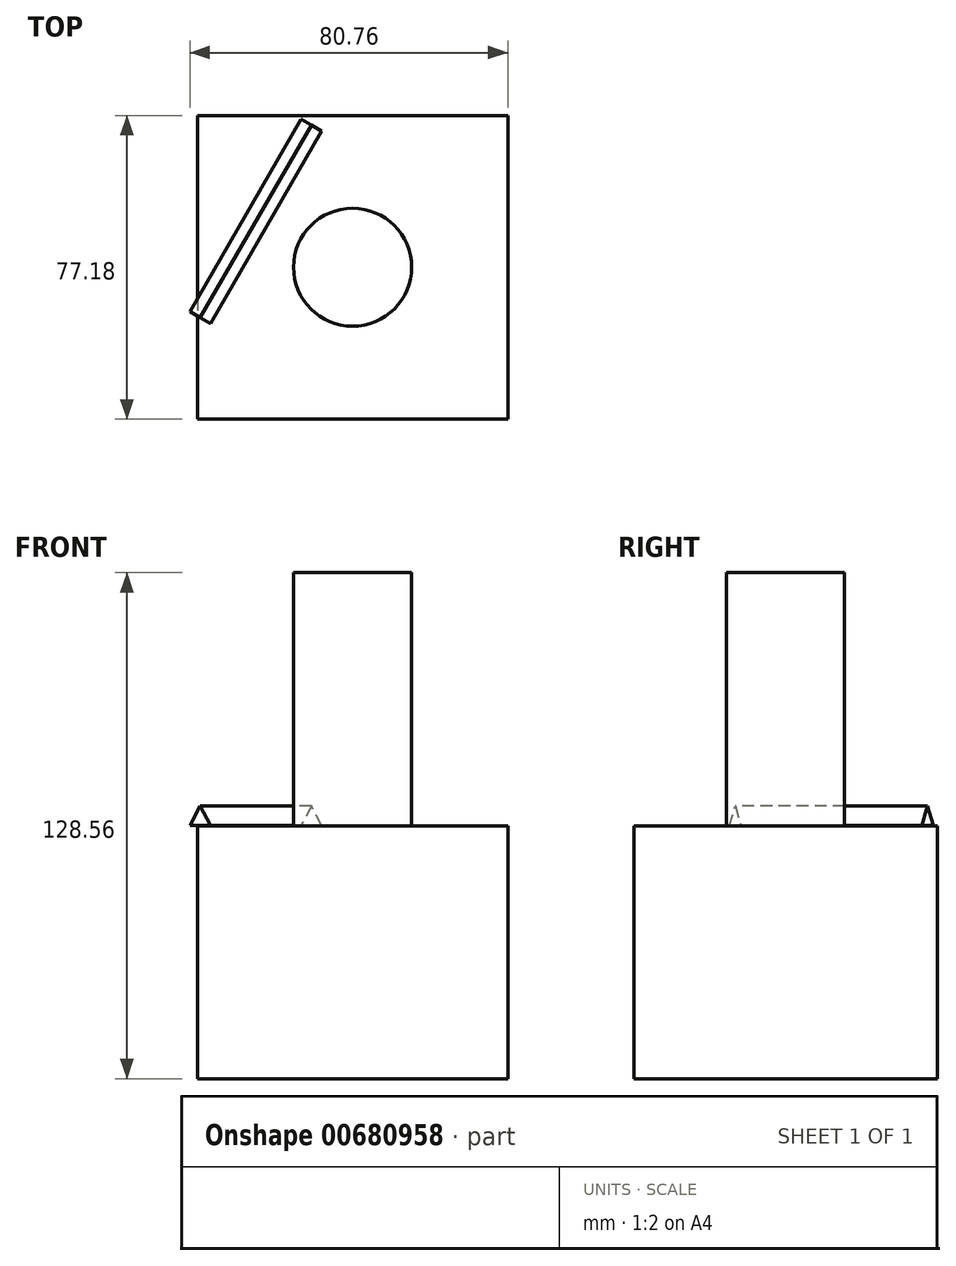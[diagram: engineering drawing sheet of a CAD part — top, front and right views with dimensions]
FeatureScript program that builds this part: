
annotation { "Feature Type Name" : "Feature", "Feature Type Description" : "" }
export const myFeature = defineFeature(function(context is Context, id is Id, definition is map)
    precondition{}
    {
        {
            var Q0;
            Q0=qCreatedBy(makeId("Top.planeOp"),FACE);
            var sketch = newSketch(context, id + "F0", { "sketchPlane" : qUnion([Q0])});
            skLineSegment(sketch, "E0.bottom", {"start": v(39.42, 38.59) * mm, "end": v(-39.42, 38.59) * mm});
            skLineSegment(sketch, "E0.top", {"start": v(39.42, -38.59) * mm, "end": v(-39.42, -38.59) * mm});
            skLineSegment(sketch, "E0.left", {"start": v(39.42, 38.59) * mm, "end": v(39.42, -38.59) * mm});
            skLineSegment(sketch, "E0.right", {"start": v(-39.42, 38.59) * mm, "end": v(-39.42, -38.59) * mm});
            skPoint(sketch, "E0.middle", {"position": v(0, 0) * mm});
            skSolve(sketch);
        }
        {
            var Q0;
            Q0=makeQuery(id+"F0.imprint","IMPRINT",FACE,{"disambiguationData":[TD([[makeQuery(id+"F0.imprint","IMPRINT",EDGE,{"derivedFrom":sQuery(id+"F0.wireOp",EDGE,"E0.bottom")}),1.0]])]});
            var Q1;
            Q1 = qSketchRegion(id + "F0", true);
            extrude(context, id + "F1", {"entities" : qUnion([Q0, Q1]), "depth" : 64.24 * mm, "offsetDistance" : 25.4 * mm});
        }
        {
            var Q0;
            Q0=makeQuery(id+"F1.opExtrude","CAP_FACE",FACE,{"disambiguationData":[OSD([sQuery(id+"F0.wireOp",EDGE,"E0.bottom"),sQuery(id+"F0.wireOp",EDGE,"E0.top"),sQuery(id+"F0.wireOp",EDGE,"E0.left"),sQuery(id+"F0.wireOp",EDGE,"E0.right")])],"isStart":false});
            var sketch = newSketch(context, id + "F2", { "sketchPlane" : qUnion([Q0])});
            skCircle(sketch, "E1", {"center": v(0, 0) * mm, "radius": 15 * mm});
            skLineSegment(sketch, "E2", {"start": v(-9.97, 38.59) * mm, "end": v(-39.42, -12.4) * mm});
            skLineSegment(sketch, "E3.MirrorCS", {"start": v(9.97, 38.59) * mm, "end": v(39.42, -12.4) * mm});
            skSolve(sketch);
        }
        {
            var Q0;
            Q0=makeQuery(id+"F2.imprint","IMPRINT",FACE,{"disambiguationData":[TD([[makeQuery(id+"F2.imprint","IMPRINT",EDGE,{"derivedFrom":sQuery(id+"F2.wireOp",EDGE,"E1")}),1.0]])]});
            extrude(context, id + "F3", {"entities" : qUnion([Q0]), "operationType" : NewBodyOperationType.ADD, "depth" : 64.32 * mm, "offsetDistance" : 25.4 * mm});
        }
        {
            var Q0;
            Q0=sQuery(id+"F2.wireOp",VERTEX,"E2.end");
            var Q1;
            Q1=sQuery(id+"F2.wireOp",EDGE,"E2");
            cPlane(context, id + "F4", {"entities" : qUnion([Q0, Q1]), "cplaneType" : CPlaneType.LINE_POINT, "offset" : 25.4 * mm, "width" : 152.4 * mm, "height" : 152.4 * mm});
        }
        {
            var Q0;
            Q0=qCreatedBy(id+"F4.planeOp",FACE);
            var sketch = newSketch(context, id + "F5", { "sketchPlane" : qUnion([Q0])});
            skLineSegment(sketch, "E4", {"start": v(-30.15, 64.3) * mm, "end": v(-24.16, 64.3) * mm});
            skLineSegment(sketch, "E5", {"start": v(-24.16, 64.3) * mm, "end": v(-27.13, 69.3) * mm});
            skLineSegment(sketch, "E6", {"start": v(-27.13, 69.3) * mm, "end": v(-30.15, 64.3) * mm});
            skSolve(sketch);
        }
        {
            var Q0;
            Q0=makeQuery(id+"F5.imprint","IMPRINT",FACE,{"disambiguationData":[TD([[makeQuery(id+"F5.imprint","IMPRINT",EDGE,{"derivedFrom":sQuery(id+"F5.wireOp",EDGE,"E4")}),1.0]])]});
            extrude(context, id + "F6", {"entities" : qUnion([Q0]), "oppositeDirection" : true, "depth" : 56.44 * mm, "offsetDistance" : 25.4 * mm});
        }
    });
